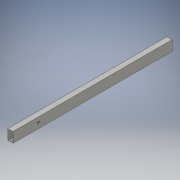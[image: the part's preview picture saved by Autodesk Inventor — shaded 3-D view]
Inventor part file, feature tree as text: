
AUTODESK INVENTOR PART (.ipt)
format: ipt  version: 2016 (Build 200138000, 138)  size: 122,880 bytes
history: native  units: in
note: dims shown in document units (in); Inventor stores cm internally (conversion verified against a paired STEP export)
features: extrude x3, sketch x3, projected_geometry x2
ambient origin geometry x8: Origin, YZ Plane, XZ Plane, XY Plane, X Axis, Y Axis, Z Axis, Center Point
bodies: Solid1 (feature_tree)
feature tree (8):
  extrude  "Extrusion1"  Depth=0.125in
  extrude  "Extrusion3"  Depth=1.0in TaperAngle=0.0deg
  extrude  "Extrusion4"  [1 undecoded]
  sketch  "Sketch1"  dims[d0=1.0in d1=2.0in d2=0.125in d3=0.125in d4=0.125in d5=0.125in d6=30.125in d7=0.0in d13=5.0in]
  sketch  "Sketch3"  dims[d14=0.5in d15=1.0in d16=0.0in]
  projected_geometry  "Projected Loop2"
  sketch  "Sketch4"  dims[d17=1.0in d18=0.0in]
  projected_geometry  "Projected Loop3"
note: 1 required parameter value undecoded (feature->parameter linkage not recoverable at this tier; creation-order binding heuristic only, values carry confidence <= 0.55)
